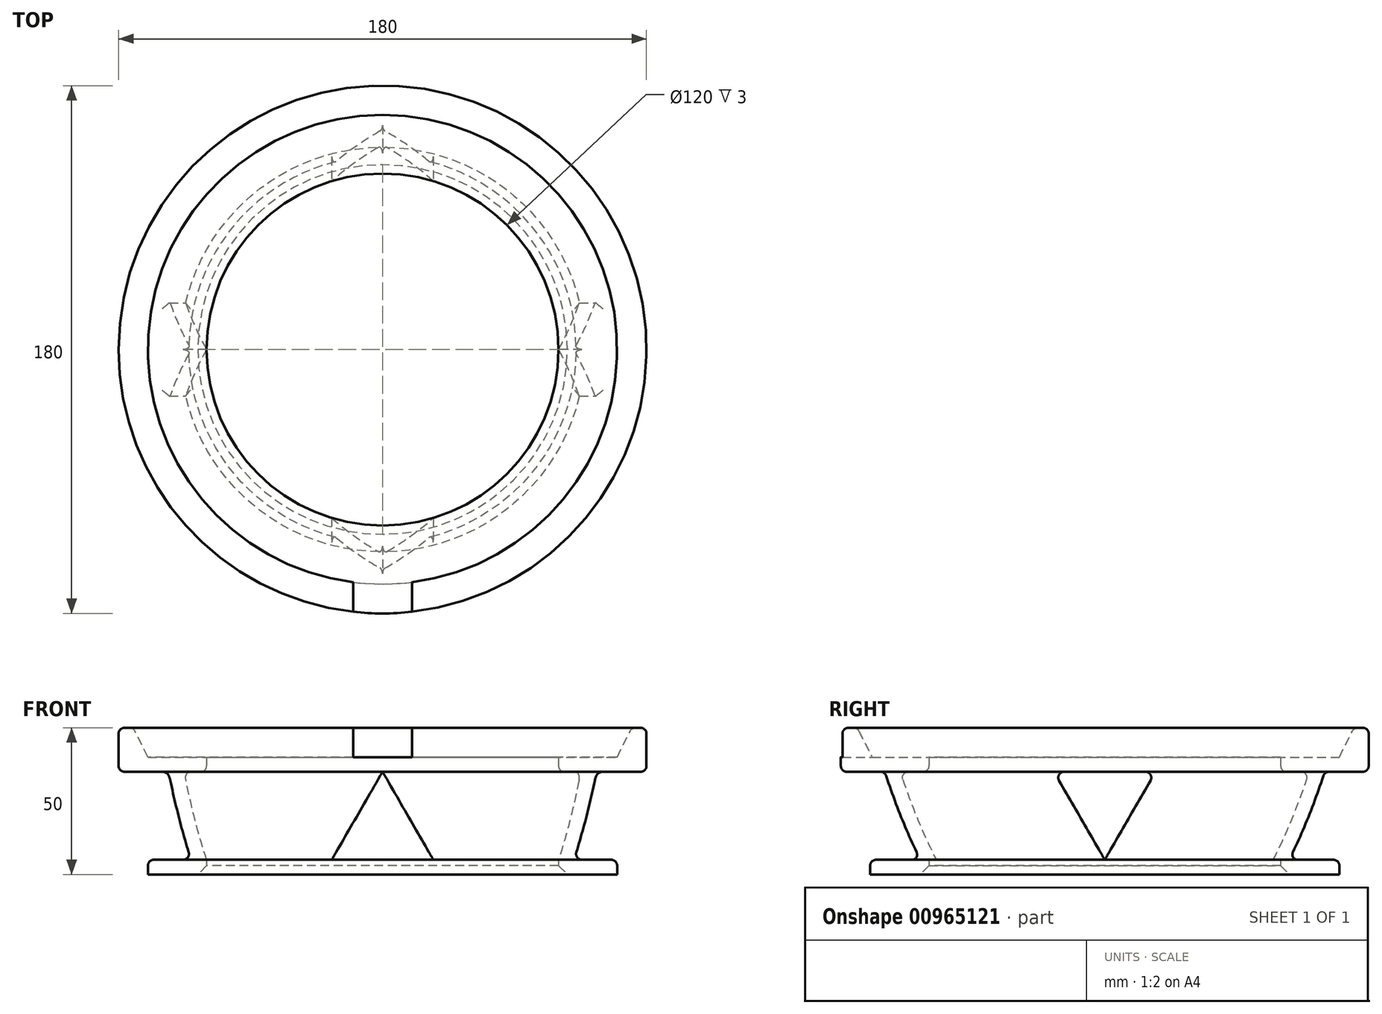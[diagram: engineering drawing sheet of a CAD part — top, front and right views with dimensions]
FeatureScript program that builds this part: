
annotation { "Feature Type Name" : "Feature", "Feature Type Description" : "" }
export const myFeature = defineFeature(function(context is Context, id is Id, definition is map)
    precondition{}
    {
        {
            var Q0;
            Q0=qCreatedBy(makeId("Front.planeOp"),FACE);
            var sketch = newSketch(context, id + "F0", { "sketchPlane" : qUnion([Q0])});
            skLineSegment(sketch, "E0.bottom", {"start": v(80, 0) * mm, "end": v(60, 0) * mm});
            skLineSegment(sketch, "E0.top", {"start": v(80, 5) * mm, "end": v(65.26, 5) * mm});
            skLineSegment(sketch, "E0.left", {"start": v(80, 0) * mm, "end": v(80, 5) * mm});
            skLineSegment(sketch, "E0.right", {"start": v(60, 0) * mm, "end": v(60, 5) * mm});
            skLineSegment(sketch, "E1.bottom", {"start": v(60, 40) * mm, "end": v(80, 40) * mm});
            skLineSegment(sketch, "E1.left", {"start": v(60, 40) * mm, "end": v(60, 35) * mm});
            skLineSegment(sketch, "E2", {"start": v(80, 40) * mm, "end": v(85, 50) * mm});
            skLineSegment(sketch, "E3", {"start": v(85, 50) * mm, "end": v(90, 50) * mm});
            skLineSegment(sketch, "E4", {"start": v(90, 50) * mm, "end": v(90, 35) * mm});
            skLineSegment(sketch, "E5", {"start": v(60, 35) * mm, "end": v(69.74, 35) * mm});
            skLineSegment(sketch, "E6", {"start": v(60, 35) * mm, "end": v(60, 5) * mm, "construction": true});
            skLineSegment(sketch, "E7", {"start": v(0, 0) * mm, "end": v(0, 40) * mm, "construction": true});
            skLineSegment(sketch, "E8", {"start": v(69.74, 35) * mm, "end": v(60, 5) * mm});
            skLineSegment(sketch, "E9", {"start": v(75, 35) * mm, "end": v(65.26, 5) * mm});
            skLineSegment(sketch, "E10.trimOffspring", {"start": v(75, 35) * mm, "end": v(90, 35) * mm});
            skSolve(sketch);
        }
        {
            var Q0;
            Q0 = qSketchRegion(id + "F0", true);
            var Q1;
            Q1=sQuery(id+"F0.wireOp",EDGE,"E7");
            revolve(context, id + "F1", {"surfaceOperationType" : NewSurfaceOperationType.NEW, "entities" : qUnion([Q0]), "axis" : qUnion([Q1]), "revolveType" : RevolveType.FULL});
        }
        {
            var Q0;
            Q0=qCreatedBy(makeId("Front.planeOp"),FACE);
            var sketch = newSketch(context, id + "F2", { "sketchPlane" : qUnion([Q0])});
            skLineSegment(sketch, "E11.0", {"start": v(90, 35) * mm, "end": v(-6, 35) * mm, "construction": true});
            skLineSegment(sketch, "E12", {"start": v(17.32, 5) * mm, "end": v(0, 35) * mm});
            skLineSegment(sketch, "E13", {"start": v(0, 35) * mm, "end": v(-17.32, 5) * mm});
            skLineSegment(sketch, "E14", {"start": v(-17.32, 5) * mm, "end": v(17.32, 5) * mm});
            skLineSegment(sketch, "E15.0", {"start": v(80, 5) * mm, "end": v(17.32, 5) * mm, "construction": true});
            skLineSegment(sketch, "E16.trimOffspring", {"start": v(-6, 35) * mm, "end": v(-90, 35) * mm, "construction": true});
            skLineSegment(sketch, "E17.trimOffspring", {"start": v(-17.32, 5) * mm, "end": v(-80, 5) * mm, "construction": true});
            skLineSegment(sketch, "E18", {"start": v(-40.64, 35) * mm, "end": v(-6, 35) * mm, "construction": true});
            skSolve(sketch);
        }
        {
            var Q0;
            Q0 = qSketchRegion(id + "F2", true);
            var Q1;
            Q1=makeQuery(id+"F1.opRevolve","SWEPT_BODY",BODY,{"disambiguationData":[OSD([sQuery(id+"F0.wireOp",EDGE,"E0.bottom"),sQuery(id+"F0.wireOp",EDGE,"E0.top"),sQuery(id+"F0.wireOp",EDGE,"E0.left"),sQuery(id+"F0.wireOp",EDGE,"E0.right"),sQuery(id+"F0.wireOp",EDGE,"E1.bottom"),sQuery(id+"F0.wireOp",EDGE,"E1.left"),sQuery(id+"F0.wireOp",EDGE,"E2"),sQuery(id+"F0.wireOp",EDGE,"E3"),sQuery(id+"F0.wireOp",EDGE,"E4"),sQuery(id+"F0.wireOp",EDGE,"E5"),sQuery(id+"F0.wireOp",EDGE,"E8"),sQuery(id+"F0.wireOp",EDGE,"E9"),sQuery(id+"F0.wireOp",EDGE,"E10.trimOffspring")])]});
            extrude(context, id + "F3", {"entities" : qUnion([Q0]), "operationType" : NewBodyOperationType.REMOVE, "oppositeDirection" : true, "depth" : 1000 * mm, "endBoundEntityBody" : qUnion([Q1]), "offsetDistance" : 25 * mm, "hasSecondDirection" : true, "secondDirectionOppositeDirection" : false, "secondDirectionDepth" : 1000 * mm});
        }
        {
            var Q0;
            Q0=qCreatedBy(makeId("Right.planeOp"),FACE);
            var sketch = newSketch(context, id + "F4", { "sketchPlane" : qUnion([Q0])});
            skLineSegment(sketch, "E19", {"start": v(-17.32, 35) * mm, "end": v(0, 5) * mm});
            skLineSegment(sketch, "E20", {"start": v(0, 5) * mm, "end": v(17.32, 35) * mm});
            skLineSegment(sketch, "E21", {"start": v(17.32, 35) * mm, "end": v(-17.32, 35) * mm});
            skLineSegment(sketch, "E22.0", {"start": v(80, 5) * mm, "end": v(-80, 5) * mm});
            skLineSegment(sketch, "E22.1", {"start": v(90, 35) * mm, "end": v(-90, 35) * mm});
            skSolve(sketch);
        }
        {
            var Q0;
            Q0 = qSketchRegion(id + "F4", true);
            extrude(context, id + "F5", {"entities" : qUnion([Q0]), "operationType" : NewBodyOperationType.REMOVE, "depth" : 1000 * mm, "offsetDistance" : 25 * mm, "hasSecondDirection" : true, "secondDirectionOppositeDirection" : true, "secondDirectionDepth" : 1000 * mm});
        }
        {
            var Q0;
            Q0=qCreatedBy(makeId("Front.planeOp"),FACE);
            var sketch = newSketch(context, id + "F6", { "sketchPlane" : qUnion([Q0])});
            skLineSegment(sketch, "E23.0", {"start": v(90, 35) * mm, "end": v(-90, 35) * mm, "construction": true});
            skLineSegment(sketch, "E23.1", {"start": v(90, 50) * mm, "end": v(10, 50) * mm, "construction": true});
            skLineSegment(sketch, "E24.0", {"start": v(60, 40) * mm, "end": v(10, 40) * mm, "construction": true});
            skLineSegment(sketch, "E25", {"start": v(10, 40) * mm, "end": v(10, 50) * mm});
            skLineSegment(sketch, "E26", {"start": v(10, 50) * mm, "end": v(0, 50) * mm});
            skLineSegment(sketch, "E27", {"start": v(0, 40) * mm, "end": v(10, 40) * mm});
            skLineSegment(sketch, "E28.MirrorCS", {"start": v(-10, 50) * mm, "end": v(0, 50) * mm});
            skLineSegment(sketch, "E29.MirrorCS", {"start": v(0, 40) * mm, "end": v(-10, 40) * mm});
            skLineSegment(sketch, "E30.MirrorCS", {"start": v(-10, 40) * mm, "end": v(-10, 50) * mm});
            skLineSegment(sketch, "E31", {"start": v(-10, 40) * mm, "end": v(-60, 40) * mm, "construction": true});
            skLineSegment(sketch, "E32", {"start": v(-10, 50) * mm, "end": v(-90, 50) * mm, "construction": true});
            skPoint(sketch, "E33.start.orphan", {"position": v(0, 50) * mm});
            skSolve(sketch);
        }
        {
            var Q0;
            Q0 = qSketchRegion(id + "F6", true);
            var Q1;
            Q1=makeQuery(id+"F1.opRevolve","SWEPT_BODY",BODY,{"disambiguationData":[OSD([sQuery(id+"F0.wireOp",EDGE,"E0.bottom"),sQuery(id+"F0.wireOp",EDGE,"E0.top"),sQuery(id+"F0.wireOp",EDGE,"E0.left"),sQuery(id+"F0.wireOp",EDGE,"E0.right"),sQuery(id+"F0.wireOp",EDGE,"E1.bottom"),sQuery(id+"F0.wireOp",EDGE,"E1.left"),sQuery(id+"F0.wireOp",EDGE,"E2"),sQuery(id+"F0.wireOp",EDGE,"E3"),sQuery(id+"F0.wireOp",EDGE,"E4"),sQuery(id+"F0.wireOp",EDGE,"E5"),sQuery(id+"F0.wireOp",EDGE,"E8"),sQuery(id+"F0.wireOp",EDGE,"E9"),sQuery(id+"F0.wireOp",EDGE,"E10.trimOffspring")])]});
            extrude(context, id + "F7", {"entities" : qUnion([Q0]), "operationType" : NewBodyOperationType.REMOVE, "endBound" : BoundingType.THROUGH_ALL, "depth" : 25 * mm, "endBoundEntityBody" : qUnion([Q1]), "offsetDistance" : 25 * mm});
        }
        {
            var Q0;
            Q0=makeQuery(id+"F1.opRevolve","SWEPT_EDGE",EDGE,{"disambiguationData":[OSD([sQuery(id+"F0.wireOp",EDGE,"E2"),sQuery(id+"F0.wireOp",EDGE,"E3")])]});
            var Q1;
            Q1=makeQuery(id+"F1.opRevolve","SWEPT_EDGE",EDGE,{"disambiguationData":[OSD([sQuery(id+"F0.wireOp",EDGE,"E3"),sQuery(id+"F0.wireOp",EDGE,"E4")])]});
            var Q2;
            Q2=makeQuery(id+"F1.opRevolve","SWEPT_EDGE",EDGE,{"disambiguationData":[OSD([sQuery(id+"F0.wireOp",EDGE,"E0.top"),sQuery(id+"F0.wireOp",EDGE,"E0.left")])]});
            var Q3;
            {var subQ0=makeQuery(id+"F3.opExtrude","SWEPT_FACE",FACE,{"disambiguationData":[OSD([sQuery(id+"F2.wireOp",EDGE,"E12")])]});var subQ1=makeQuery(id+"F3.boolean.opBoolean","COPY",FACE,{"disambiguationData":[OD(0.0)],"derivedFrom":subQ0});var subQ2=sQuery(id+"F0.wireOp",EDGE,"E0.top");var subQ4=sQuery(id+"F0.wireOp",EDGE,"E9");Q3=makeQuery(id+"FpFSd6qXAehcpU0_1.-4.F5.boolean.opBoolean","SPLIT",EDGE,{"disambiguationData":[TD([subQ1])],"derivedFrom":makeQuery(id+"FgNUQvb7w6E0jcb_1.-5.F3.boolean.opBoolean","SPLIT",EDGE,{"disambiguationData":[TD([subQ1])],"derivedFrom":makeQuery(id+"F3.boolean.opBoolean","SPLIT",EDGE,{"disambiguationData":[TD([subQ0])],"derivedFrom":makeQuery(id+"F1.opRevolve","SWEPT_EDGE",EDGE,{"disambiguationData":[OSD([subQ2,subQ4])]})})})});}
            var Q4;
            {var subQ0=sQuery(id+"F0.wireOp",EDGE,"E0.top");var subQ2=makeQuery(id+"FgNUQvb7w6E0jcb_1.-5.F3.opExtrude","SWEPT_FACE",FACE,{"disambiguationData":[OSD([sQuery(id+"F2.wireOp",EDGE,"E13")])]});var subQ3=sQuery(id+"F0.wireOp",EDGE,"E9");var subQ5=makeQuery(id+"F3.opExtrude","SWEPT_FACE",FACE,{"disambiguationData":[OSD([sQuery(id+"F2.wireOp",EDGE,"E12")])]});Q4=makeQuery(id+"FpFSd6qXAehcpU0_1.-4.F5.boolean.opBoolean","SPLIT",EDGE,{"disambiguationData":[TD([makeQuery(id+"FgNUQvb7w6E0jcb_1.-5.F3.boolean.opBoolean","COPY",FACE,{"disambiguationData":[OD(1.0)],"derivedFrom":subQ2})])],"derivedFrom":makeQuery(id+"FgNUQvb7w6E0jcb_1.-5.F3.boolean.opBoolean","SPLIT",EDGE,{"disambiguationData":[TD([makeQuery(id+"F3.boolean.opBoolean","COPY",FACE,{"disambiguationData":[OD(0.0)],"derivedFrom":subQ5})])],"derivedFrom":makeQuery(id+"F3.boolean.opBoolean","SPLIT",EDGE,{"disambiguationData":[TD([subQ5])],"derivedFrom":makeQuery(id+"F1.opRevolve","SWEPT_EDGE",EDGE,{"disambiguationData":[OSD([subQ0,subQ3])]})})})});}
            var Q5;
            {var subQ0=sQuery(id+"F2.wireOp",EDGE,"E13");var subQ1=makeQuery(id+"F3.opExtrude","SWEPT_FACE",FACE,{"disambiguationData":[OSD([subQ0])]});var subQ2=makeQuery(id+"F3.boolean.opBoolean","COPY",FACE,{"disambiguationData":[OD(0.0)],"derivedFrom":subQ1});var subQ3=sQuery(id+"F0.wireOp",EDGE,"E9");var subQ5=sQuery(id+"F0.wireOp",EDGE,"E0.top");Q5=makeQuery(id+"FpFSd6qXAehcpU0_1.-5.F5.boolean.opBoolean","SPLIT",EDGE,{"disambiguationData":[TD([subQ2])],"derivedFrom":makeQuery(id+"FgNUQvb7w6E0jcb_1.-4.F3.boolean.opBoolean","SPLIT",EDGE,{"disambiguationData":[TD([subQ2])],"derivedFrom":makeQuery(id+"FgNUQvb7w6E0jcb_1.-5.F3.boolean.opBoolean","SPLIT",EDGE,{"disambiguationData":[TD([subQ2])],"derivedFrom":makeQuery(id+"F3.boolean.opBoolean","SPLIT",EDGE,{"disambiguationData":[TD([subQ1])],"derivedFrom":makeQuery(id+"F1.opRevolve","SWEPT_EDGE",EDGE,{"disambiguationData":[OSD([subQ5,subQ3])]})})})})});}
            var Q6;
            {var subQ0=sQuery(id+"F2.wireOp",EDGE,"E13");var subQ1=makeQuery(id+"FgNUQvb7w6E0jcb_1.-4.F3.opExtrude","SWEPT_FACE",FACE,{"disambiguationData":[OSD([subQ0])]});var subQ2=sQuery(id+"F0.wireOp",EDGE,"E0.top");var subQ4=sQuery(id+"F0.wireOp",EDGE,"E9");var subQ6=makeQuery(id+"F3.opExtrude","SWEPT_FACE",FACE,{"disambiguationData":[OSD([subQ0])]});var subQ7=makeQuery(id+"F3.boolean.opBoolean","COPY",FACE,{"disambiguationData":[OD(0.0)],"derivedFrom":subQ6});Q6=makeQuery(id+"FpFSd6qXAehcpU0_1.-5.F5.boolean.opBoolean","SPLIT",EDGE,{"disambiguationData":[TD([makeQuery(id+"FgNUQvb7w6E0jcb_1.-4.F3.boolean.opBoolean","COPY",FACE,{"disambiguationData":[OD(0.0)],"derivedFrom":subQ1})])],"derivedFrom":makeQuery(id+"FgNUQvb7w6E0jcb_1.-4.F3.boolean.opBoolean","SPLIT",EDGE,{"disambiguationData":[TD([subQ7])],"derivedFrom":makeQuery(id+"FgNUQvb7w6E0jcb_1.-5.F3.boolean.opBoolean","SPLIT",EDGE,{"disambiguationData":[TD([subQ7])],"derivedFrom":makeQuery(id+"F3.boolean.opBoolean","SPLIT",EDGE,{"disambiguationData":[TD([subQ6])],"derivedFrom":makeQuery(id+"F1.opRevolve","SWEPT_EDGE",EDGE,{"disambiguationData":[OSD([subQ2,subQ4])]})})})})});}
            var Q7;
            {var subQ0=makeQuery(id+"FgNUQvb7w6E0jcb_1.-4.F3.opExtrude","SWEPT_FACE",FACE,{"disambiguationData":[OSD([sQuery(id+"F2.wireOp",EDGE,"E12")])]});var subQ1=sQuery(id+"F0.wireOp",EDGE,"E9");var subQ3=sQuery(id+"F0.wireOp",EDGE,"E0.top");var subQ5=sQuery(id+"F2.wireOp",EDGE,"E13");var subQ6=makeQuery(id+"FgNUQvb7w6E0jcb_1.-5.F3.opExtrude","SWEPT_FACE",FACE,{"disambiguationData":[OSD([subQ5])]});var subQ8=makeQuery(id+"F3.opExtrude","SWEPT_FACE",FACE,{"disambiguationData":[OSD([subQ5])]});Q7=makeQuery(id+"F5.boolean.opBoolean","SPLIT",EDGE,{"disambiguationData":[TD([makeQuery(id+"FgNUQvb7w6E0jcb_1.-4.F3.boolean.opBoolean","COPY",FACE,{"disambiguationData":[OD(0.0)],"derivedFrom":subQ0})])],"derivedFrom":makeQuery(id+"FgNUQvb7w6E0jcb_1.-4.F3.boolean.opBoolean","SPLIT",EDGE,{"disambiguationData":[TD([makeQuery(id+"FgNUQvb7w6E0jcb_1.-5.F3.boolean.opBoolean","COPY",FACE,{"disambiguationData":[OD(0.0)],"derivedFrom":subQ6})])],"derivedFrom":makeQuery(id+"FgNUQvb7w6E0jcb_1.-5.F3.boolean.opBoolean","SPLIT",EDGE,{"disambiguationData":[TD([makeQuery(id+"F3.boolean.opBoolean","COPY",FACE,{"disambiguationData":[OD(0.0)],"derivedFrom":subQ8})])],"derivedFrom":makeQuery(id+"F3.boolean.opBoolean","SPLIT",EDGE,{"disambiguationData":[TD([subQ8])],"derivedFrom":makeQuery(id+"F1.opRevolve","SWEPT_EDGE",EDGE,{"disambiguationData":[OSD([subQ3,subQ1])]})})})})});}
            var Q8;
            {var subQ0=sQuery(id+"F2.wireOp",EDGE,"E13");var subQ1=makeQuery(id+"FgNUQvb7w6E0jcb_1.-5.F3.opExtrude","SWEPT_FACE",FACE,{"disambiguationData":[OSD([subQ0])]});var subQ2=makeQuery(id+"FgNUQvb7w6E0jcb_1.-5.F3.boolean.opBoolean","COPY",FACE,{"disambiguationData":[OD(0.0)],"derivedFrom":subQ1});var subQ3=sQuery(id+"F0.wireOp",EDGE,"E9");var subQ5=sQuery(id+"F0.wireOp",EDGE,"E0.top");var subQ8=makeQuery(id+"F3.opExtrude","SWEPT_FACE",FACE,{"disambiguationData":[OSD([subQ0])]});Q8=makeQuery(id+"F5.boolean.opBoolean","SPLIT",EDGE,{"disambiguationData":[TD([subQ2])],"derivedFrom":makeQuery(id+"FgNUQvb7w6E0jcb_1.-4.F3.boolean.opBoolean","SPLIT",EDGE,{"disambiguationData":[TD([subQ2])],"derivedFrom":makeQuery(id+"FgNUQvb7w6E0jcb_1.-5.F3.boolean.opBoolean","SPLIT",EDGE,{"disambiguationData":[TD([makeQuery(id+"F3.boolean.opBoolean","COPY",FACE,{"disambiguationData":[OD(0.0)],"derivedFrom":subQ8})])],"derivedFrom":makeQuery(id+"F3.boolean.opBoolean","SPLIT",EDGE,{"disambiguationData":[TD([subQ8])],"derivedFrom":makeQuery(id+"F1.opRevolve","SWEPT_EDGE",EDGE,{"disambiguationData":[OSD([subQ5,subQ3])]})})})})});}
            var Q9;
            {var subQ0=sQuery(id+"F0.wireOp",EDGE,"E0.top");var subQ2=makeQuery(id+"F3.opExtrude","SWEPT_FACE",FACE,{"disambiguationData":[OSD([sQuery(id+"F2.wireOp",EDGE,"E13")])]});var subQ3=makeQuery(id+"F3.boolean.opBoolean","COPY",FACE,{"disambiguationData":[OD(1.0)],"derivedFrom":subQ2});var subQ4=sQuery(id+"F0.wireOp",EDGE,"E9");Q9=makeQuery(id+"FpFSd6qXAehcpU0_1.-4.F5.boolean.opBoolean","SPLIT",EDGE,{"disambiguationData":[TD([subQ3])],"derivedFrom":makeQuery(id+"FgNUQvb7w6E0jcb_1.-5.F3.boolean.opBoolean","SPLIT",EDGE,{"disambiguationData":[TD([subQ3])],"derivedFrom":makeQuery(id+"F3.boolean.opBoolean","SPLIT",EDGE,{"disambiguationData":[TD([subQ2])],"derivedFrom":makeQuery(id+"F1.opRevolve","SWEPT_EDGE",EDGE,{"disambiguationData":[OSD([subQ0,subQ4])]})})})});}
            var Q10;
            {var subQ0=sQuery(id+"F0.wireOp",EDGE,"E0.top");var subQ2=makeQuery(id+"FgNUQvb7w6E0jcb_1.-5.F3.opExtrude","SWEPT_FACE",FACE,{"disambiguationData":[OSD([sQuery(id+"F2.wireOp",EDGE,"E12")])]});var subQ3=sQuery(id+"F0.wireOp",EDGE,"E9");var subQ5=makeQuery(id+"F3.opExtrude","SWEPT_FACE",FACE,{"disambiguationData":[OSD([sQuery(id+"F2.wireOp",EDGE,"E13")])]});Q10=makeQuery(id+"FpFSd6qXAehcpU0_1.-4.F5.boolean.opBoolean","SPLIT",EDGE,{"disambiguationData":[TD([makeQuery(id+"FgNUQvb7w6E0jcb_1.-5.F3.boolean.opBoolean","COPY",FACE,{"disambiguationData":[OD(0.0)],"derivedFrom":subQ2})])],"derivedFrom":makeQuery(id+"FgNUQvb7w6E0jcb_1.-5.F3.boolean.opBoolean","SPLIT",EDGE,{"disambiguationData":[TD([makeQuery(id+"F3.boolean.opBoolean","COPY",FACE,{"disambiguationData":[OD(1.0)],"derivedFrom":subQ5})])],"derivedFrom":makeQuery(id+"F3.boolean.opBoolean","SPLIT",EDGE,{"disambiguationData":[TD([subQ5])],"derivedFrom":makeQuery(id+"F1.opRevolve","SWEPT_EDGE",EDGE,{"disambiguationData":[OSD([subQ0,subQ3])]})})})});}
            var Q11;
            {var subQ0=sQuery(id+"F2.wireOp",EDGE,"E12");var subQ1=makeQuery(id+"FgNUQvb7w6E0jcb_1.-4.F3.opExtrude","SWEPT_FACE",FACE,{"disambiguationData":[OSD([subQ0])]});var subQ2=sQuery(id+"F0.wireOp",EDGE,"E9");var subQ4=sQuery(id+"F0.wireOp",EDGE,"E0.top");var subQ6=makeQuery(id+"F3.opExtrude","SWEPT_FACE",FACE,{"disambiguationData":[OSD([subQ0])]});var subQ7=makeQuery(id+"F3.boolean.opBoolean","COPY",FACE,{"disambiguationData":[OD(1.0)],"derivedFrom":subQ6});Q11=makeQuery(id+"FpFSd6qXAehcpU0_1.-5.F5.boolean.opBoolean","SPLIT",EDGE,{"disambiguationData":[TD([makeQuery(id+"FgNUQvb7w6E0jcb_1.-4.F3.boolean.opBoolean","COPY",FACE,{"disambiguationData":[OD(1.0)],"derivedFrom":subQ1})])],"derivedFrom":makeQuery(id+"FgNUQvb7w6E0jcb_1.-4.F3.boolean.opBoolean","SPLIT",EDGE,{"disambiguationData":[TD([subQ7])],"derivedFrom":makeQuery(id+"FgNUQvb7w6E0jcb_1.-5.F3.boolean.opBoolean","SPLIT",EDGE,{"disambiguationData":[TD([subQ7])],"derivedFrom":makeQuery(id+"F3.boolean.opBoolean","SPLIT",EDGE,{"disambiguationData":[TD([subQ6])],"derivedFrom":makeQuery(id+"F1.opRevolve","SWEPT_EDGE",EDGE,{"disambiguationData":[OSD([subQ4,subQ2])]})})})})});}
            var Q12;
            {var subQ0=sQuery(id+"F2.wireOp",EDGE,"E12");var subQ1=makeQuery(id+"F3.opExtrude","SWEPT_FACE",FACE,{"disambiguationData":[OSD([subQ0])]});var subQ2=makeQuery(id+"F3.boolean.opBoolean","COPY",FACE,{"disambiguationData":[OD(1.0)],"derivedFrom":subQ1});var subQ3=sQuery(id+"F0.wireOp",EDGE,"E9");var subQ5=sQuery(id+"F0.wireOp",EDGE,"E0.top");Q12=makeQuery(id+"FpFSd6qXAehcpU0_1.-5.F5.boolean.opBoolean","SPLIT",EDGE,{"disambiguationData":[TD([subQ2])],"derivedFrom":makeQuery(id+"FgNUQvb7w6E0jcb_1.-4.F3.boolean.opBoolean","SPLIT",EDGE,{"disambiguationData":[TD([subQ2])],"derivedFrom":makeQuery(id+"FgNUQvb7w6E0jcb_1.-5.F3.boolean.opBoolean","SPLIT",EDGE,{"disambiguationData":[TD([subQ2])],"derivedFrom":makeQuery(id+"F3.boolean.opBoolean","SPLIT",EDGE,{"disambiguationData":[TD([subQ1])],"derivedFrom":makeQuery(id+"F1.opRevolve","SWEPT_EDGE",EDGE,{"disambiguationData":[OSD([subQ5,subQ3])]})})})})});}
            var Q13;
            {var subQ0=makeQuery(id+"FgNUQvb7w6E0jcb_1.-4.F3.opExtrude","SWEPT_FACE",FACE,{"disambiguationData":[OSD([sQuery(id+"F2.wireOp",EDGE,"E13")])]});var subQ1=sQuery(id+"F0.wireOp",EDGE,"E9");var subQ3=sQuery(id+"F0.wireOp",EDGE,"E0.top");var subQ5=sQuery(id+"F2.wireOp",EDGE,"E12");var subQ6=makeQuery(id+"FgNUQvb7w6E0jcb_1.-5.F3.opExtrude","SWEPT_FACE",FACE,{"disambiguationData":[OSD([subQ5])]});var subQ8=makeQuery(id+"F3.opExtrude","SWEPT_FACE",FACE,{"disambiguationData":[OSD([subQ5])]});Q13=makeQuery(id+"F5.boolean.opBoolean","SPLIT",EDGE,{"disambiguationData":[TD([makeQuery(id+"FgNUQvb7w6E0jcb_1.-4.F3.boolean.opBoolean","COPY",FACE,{"disambiguationData":[OD(1.0)],"derivedFrom":subQ0})])],"derivedFrom":makeQuery(id+"FgNUQvb7w6E0jcb_1.-4.F3.boolean.opBoolean","SPLIT",EDGE,{"disambiguationData":[TD([makeQuery(id+"FgNUQvb7w6E0jcb_1.-5.F3.boolean.opBoolean","COPY",FACE,{"disambiguationData":[OD(1.0)],"derivedFrom":subQ6})])],"derivedFrom":makeQuery(id+"FgNUQvb7w6E0jcb_1.-5.F3.boolean.opBoolean","SPLIT",EDGE,{"disambiguationData":[TD([makeQuery(id+"F3.boolean.opBoolean","COPY",FACE,{"disambiguationData":[OD(1.0)],"derivedFrom":subQ8})])],"derivedFrom":makeQuery(id+"F3.boolean.opBoolean","SPLIT",EDGE,{"disambiguationData":[TD([subQ8])],"derivedFrom":makeQuery(id+"F1.opRevolve","SWEPT_EDGE",EDGE,{"disambiguationData":[OSD([subQ3,subQ1])]})})})})});}
            var Q14;
            {var subQ0=sQuery(id+"F2.wireOp",EDGE,"E12");var subQ1=makeQuery(id+"FgNUQvb7w6E0jcb_1.-5.F3.opExtrude","SWEPT_FACE",FACE,{"disambiguationData":[OSD([subQ0])]});var subQ2=makeQuery(id+"FgNUQvb7w6E0jcb_1.-5.F3.boolean.opBoolean","COPY",FACE,{"disambiguationData":[OD(1.0)],"derivedFrom":subQ1});var subQ3=sQuery(id+"F0.wireOp",EDGE,"E9");var subQ5=sQuery(id+"F0.wireOp",EDGE,"E0.top");var subQ8=makeQuery(id+"F3.opExtrude","SWEPT_FACE",FACE,{"disambiguationData":[OSD([subQ0])]});Q14=makeQuery(id+"F5.boolean.opBoolean","SPLIT",EDGE,{"disambiguationData":[TD([subQ2])],"derivedFrom":makeQuery(id+"FgNUQvb7w6E0jcb_1.-4.F3.boolean.opBoolean","SPLIT",EDGE,{"disambiguationData":[TD([subQ2])],"derivedFrom":makeQuery(id+"FgNUQvb7w6E0jcb_1.-5.F3.boolean.opBoolean","SPLIT",EDGE,{"disambiguationData":[TD([makeQuery(id+"F3.boolean.opBoolean","COPY",FACE,{"disambiguationData":[OD(1.0)],"derivedFrom":subQ8})])],"derivedFrom":makeQuery(id+"F3.boolean.opBoolean","SPLIT",EDGE,{"disambiguationData":[TD([subQ8])],"derivedFrom":makeQuery(id+"F1.opRevolve","SWEPT_EDGE",EDGE,{"disambiguationData":[OSD([subQ5,subQ3])]})})})})});}
            var Q15;
            {var subQ0=sQuery(id+"F0.wireOp",EDGE,"E10.trimOffspring");var subQ2=sQuery(id+"F2.wireOp",EDGE,"E12");var subQ3=makeQuery(id+"F3.boolean.opBoolean","COPY",FACE,{"disambiguationData":[OD(0.0)],"derivedFrom":makeQuery(id+"F3.opExtrude","SWEPT_FACE",FACE,{"disambiguationData":[OSD([subQ2])]})});var subQ4=sQuery(id+"F0.wireOp",EDGE,"E9");Q15=makeQuery(id+"FpFSd6qXAehcpU0_1.-4.F5.boolean.opBoolean","SPLIT",EDGE,{"disambiguationData":[TD([subQ3])],"derivedFrom":makeQuery(id+"FgNUQvb7w6E0jcb_1.-5.F3.boolean.opBoolean","SPLIT",EDGE,{"disambiguationData":[TD([subQ3])],"derivedFrom":makeQuery(id+"F3.boolean.opBoolean","SPLIT",EDGE,{"disambiguationData":[OD(1.0)],"derivedFrom":makeQuery(id+"F1.opRevolve","SWEPT_EDGE",EDGE,{"disambiguationData":[OSD([subQ4,subQ0])]})})})});}
            var Q16;
            {var subQ0=sQuery(id+"F4.wireOp",EDGE,"E22.1");Q16=makeQuery(id+"FpFSd6qXAehcpU0_1.-4.F5.boolean.opBoolean","MERGE",FACE,{"derivedFrom":[makeQuery(id+"FpFSd6qXAehcpU0_1.-5.F5.boolean.opBoolean","MERGE",FACE,{"derivedFrom":[makeQuery(id+"F5.boolean.opBoolean","MERGE",FACE,{"derivedFrom":[makeQuery(id+"F1.opRevolve","SWEPT_FACE",FACE,{"disambiguationData":[OSD([sQuery(id+"F0.wireOp",EDGE,"E5")])]}),makeQuery(id+"F1.opRevolve","SWEPT_FACE",FACE,{"disambiguationData":[OSD([sQuery(id+"F0.wireOp",EDGE,"E10.trimOffspring")])]})],"fromTools":[makeQuery(id+"F5.opExtrude","SWEPT_FACE",FACE,{"disambiguationData":[OSD([subQ0])]})]})],"fromTools":[makeQuery(id+"FpFSd6qXAehcpU0_1.-5.F5.opExtrude","SWEPT_FACE",FACE,{"disambiguationData":[OSD([subQ0])]})]})],"fromTools":[makeQuery(id+"FpFSd6qXAehcpU0_1.-4.F5.opExtrude","SWEPT_FACE",FACE,{"disambiguationData":[OSD([subQ0])]})]});}
            fillet(context, id + "F8", {"entities" : qUnion([Q0, Q1, Q2, Q3, Q4, Q5, Q6, Q7, Q8, Q9, Q10, Q11, Q12, Q13, Q14, Q15, Q16]), "radius" : 2 * mm, "tangentPropagation" : true, "allowEdgeOverflow" : false});
        }
        {
            var Q0;
            Q0=makeQuery(id+"F1.opRevolve","SWEPT_EDGE",EDGE,{"disambiguationData":[OSD([sQuery(id+"F0.wireOp",EDGE,"E0.bottom"),sQuery(id+"F0.wireOp",EDGE,"E0.right")])]});
            chamfer(context, id + "F9", {"entities" : qUnion([Q0]), "width" : 3 * mm, "tangentPropagation" : true});
        }
    });
